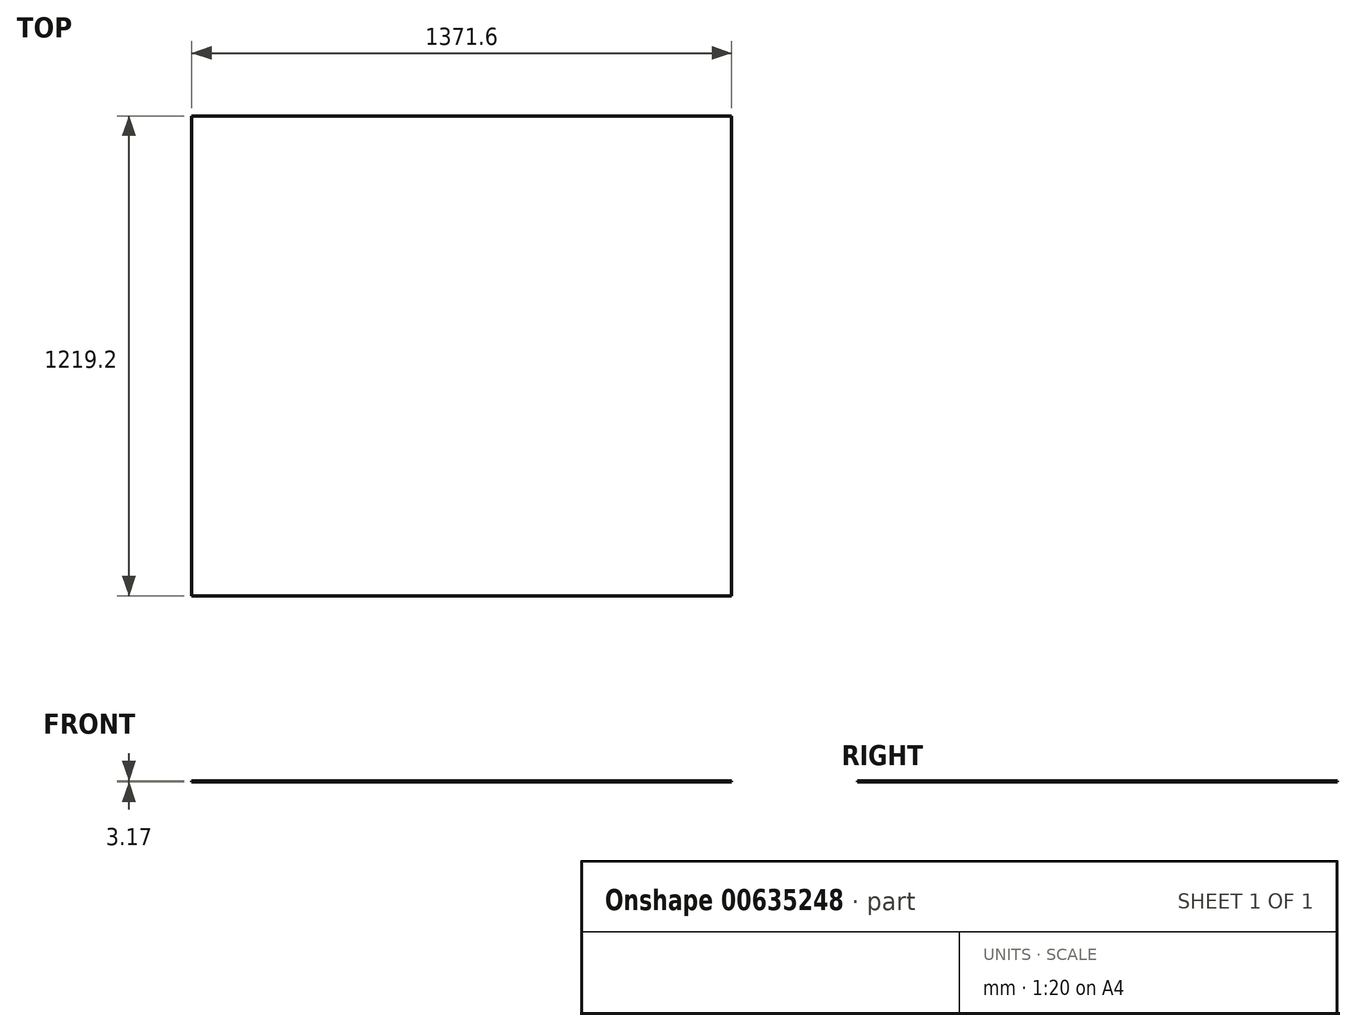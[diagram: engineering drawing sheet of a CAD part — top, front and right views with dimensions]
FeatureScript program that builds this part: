
annotation { "Feature Type Name" : "Feature", "Feature Type Description" : "" }
export const myFeature = defineFeature(function(context is Context, id is Id, definition is map)
    precondition{}
    {
        {
            var Q0;
            Q0=qCreatedBy(makeId("Top.planeOp"),FACE);
            var sketch = newSketch(context, id + "F0", { "sketchPlane" : qUnion([Q0])});
            skLineSegment(sketch, "E0.bottom", {"start": v(685.8, 609.6) * mm, "end": v(-685.8, 609.6) * mm});
            skLineSegment(sketch, "E0.top", {"start": v(685.8, -609.6) * mm, "end": v(-685.8, -609.6) * mm});
            skLineSegment(sketch, "E0.left", {"start": v(685.8, 609.6) * mm, "end": v(685.8, -609.6) * mm});
            skLineSegment(sketch, "E0.right", {"start": v(-685.8, 609.6) * mm, "end": v(-685.8, -609.6) * mm});
            skPoint(sketch, "E0.middle", {"position": v(0, 0) * mm});
            skSolve(sketch);
        }
        {
            var Q0;
            Q0 = qSketchRegion(id + "F0", true);
            extrude(context, id + "F1", {"entities" : qUnion([Q0]), "depth" : 3.17 * mm, "offsetDistance" : 25.4 * mm});
        }
    });
